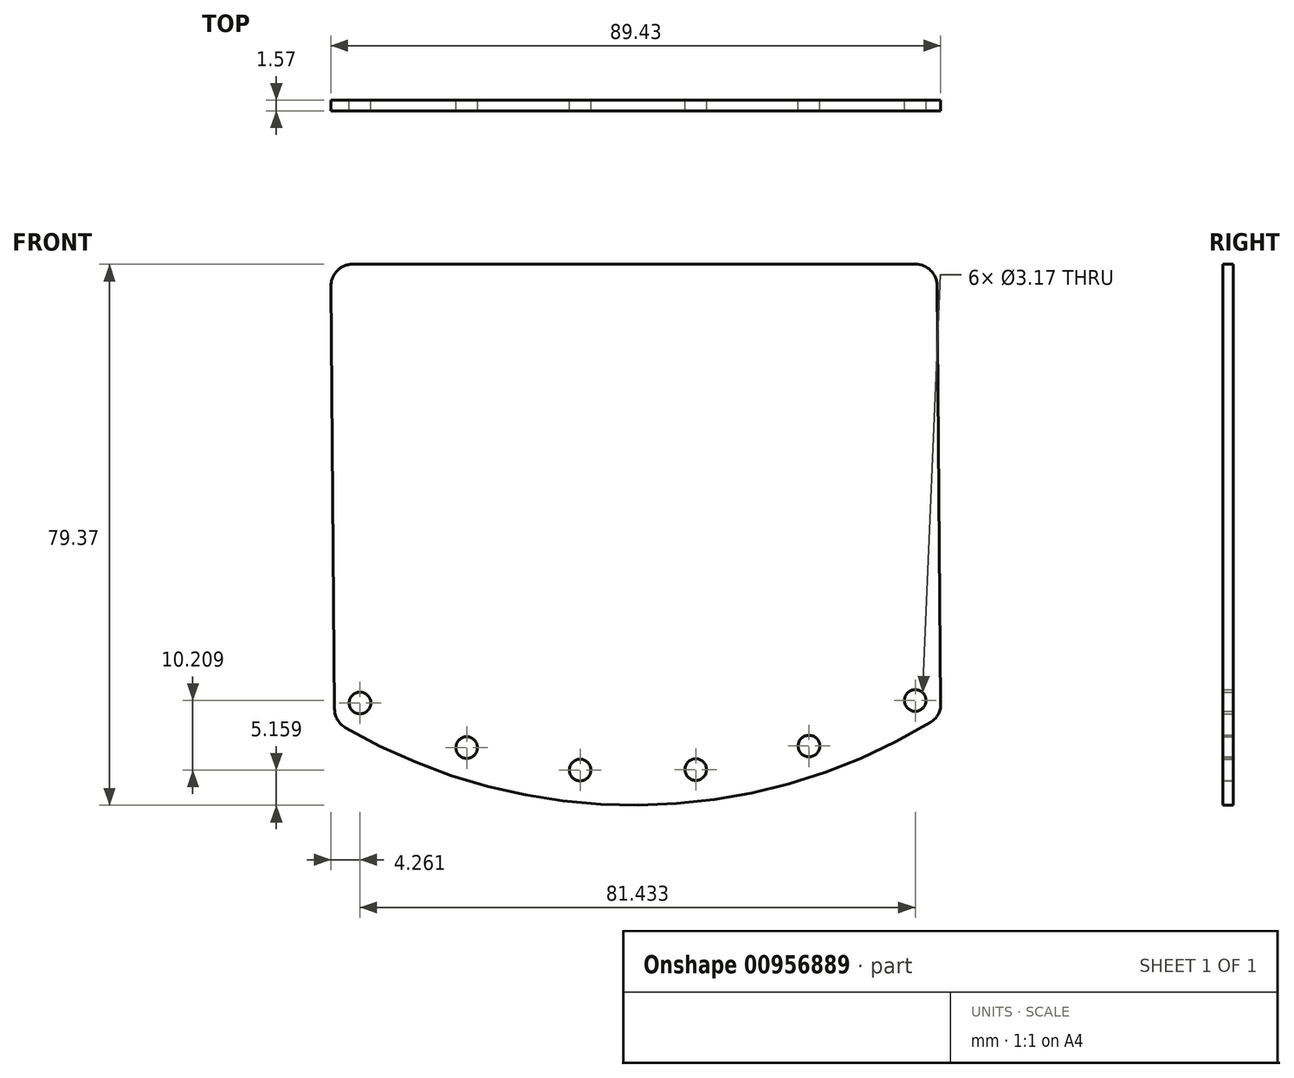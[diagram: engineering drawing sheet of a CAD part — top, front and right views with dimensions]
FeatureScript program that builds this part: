
annotation { "Feature Type Name" : "Feature", "Feature Type Description" : "" }
export const myFeature = defineFeature(function(context is Context, id is Id, definition is map)
    precondition{}
    {
        {
            var Q0;
            Q0=qCreatedBy(makeId("Front.planeOp"),FACE);
            var sketch = newSketch(context, id + "F0", { "sketchPlane" : qUnion([Q0])});
            skLineSegment(sketch, "E0.bottom", {"start": v(-45.52, 33.87) * mm, "end": v(37.03, 33.87) * mm});
            skLineSegment(sketch, "E0.left", {"start": v(-48.7, 30.67) * mm, "end": v(-48.16, -31.4) * mm});
            skLineSegment(sketch, "E0.right", {"start": v(40.2, 30.72) * mm, "end": v(40.73, -30.63) * mm});
            skPoint(sketch, "E1.startSnap0", {"position": v(-4.27, 33.87) * mm});
            skArc(sketch, "E2", {"start": v(-46.59, -34.11) * mm, "mid": v(-3.6, -45.5) * mm, "end": v(39.2, -33.38) * mm});
            skPoint(sketch, "E3.visualSharp", {"position": v(-48.72, 33.87) * mm});
            skArc(sketch, "E3.filletArc", {"start": v(-45.52, 33.87) * mm, "mid": v(-47.78, 32.93) * mm, "end": v(-48.7, 30.67) * mm});
            skPoint(sketch, "E4.visualSharp", {"position": v(40.18, 33.87) * mm});
            skArc(sketch, "E4.filletArc", {"start": v(40.2, 30.72) * mm, "mid": v(39.27, 32.95) * mm, "end": v(37.03, 33.87) * mm});
            skCircle(sketch, "E5", {"center": v(37, -30.13) * mm, "radius": 1.59 * mm});
            skCircle(sketch, "E6.1.0", {"center": v(21.4, -36.82) * mm, "radius": 1.59 * mm});
            skCircle(sketch, "E6.2.0", {"center": v(4.8, -40.27) * mm, "radius": 1.59 * mm});
            skCircle(sketch, "E6.3.0", {"center": v(-12.16, -40.34) * mm, "radius": 1.59 * mm});
            skCircle(sketch, "E6.4.0", {"center": v(-28.8, -37.04) * mm, "radius": 1.59 * mm});
            skCircle(sketch, "E6.5.0", {"center": v(-44.44, -30.5) * mm, "radius": 1.59 * mm});
            skPoint(sketch, "E6.center", {"position": v(-4.06, 44.08) * mm});
            skLineSegment(sketch, "E6.anchor1", {"start": v(-4.06, 44.08) * mm, "end": v(37, -30.13) * mm, "construction": true});
            skLineSegment(sketch, "E6.anchor2", {"start": v(-4.06, 44.08) * mm, "end": v(-44.44, -30.5) * mm, "construction": true});
            skPoint(sketch, "E7.visualSharp", {"position": v(-48.15, -33.18) * mm});
            skArc(sketch, "E7.filletArc", {"start": v(-48.16, -31.4) * mm, "mid": v(-47.74, -32.96) * mm, "end": v(-46.59, -34.11) * mm});
            skPoint(sketch, "E8.visualSharp", {"position": v(40.75, -32.42) * mm});
            skArc(sketch, "E8.filletArc", {"start": v(39.2, -33.38) * mm, "mid": v(40.33, -32.2) * mm, "end": v(40.73, -30.63) * mm});
            skSolve(sketch);
        }
        {
            var Q0;
            Q0=makeQuery(id+"F0.imprint","IMPRINT",FACE,{"disambiguationData":[TD([[makeQuery(id+"F0.imprint","IMPRINT",EDGE,{"derivedFrom":sQuery(id+"F0.wireOp",EDGE,"E0.bottom")}),-1.0]])]});
            extrude(context, id + "F1", {"entities" : qUnion([Q0]), "depth" : 1.57 * mm, "offsetDistance" : 25.4 * mm});
        }
    });
